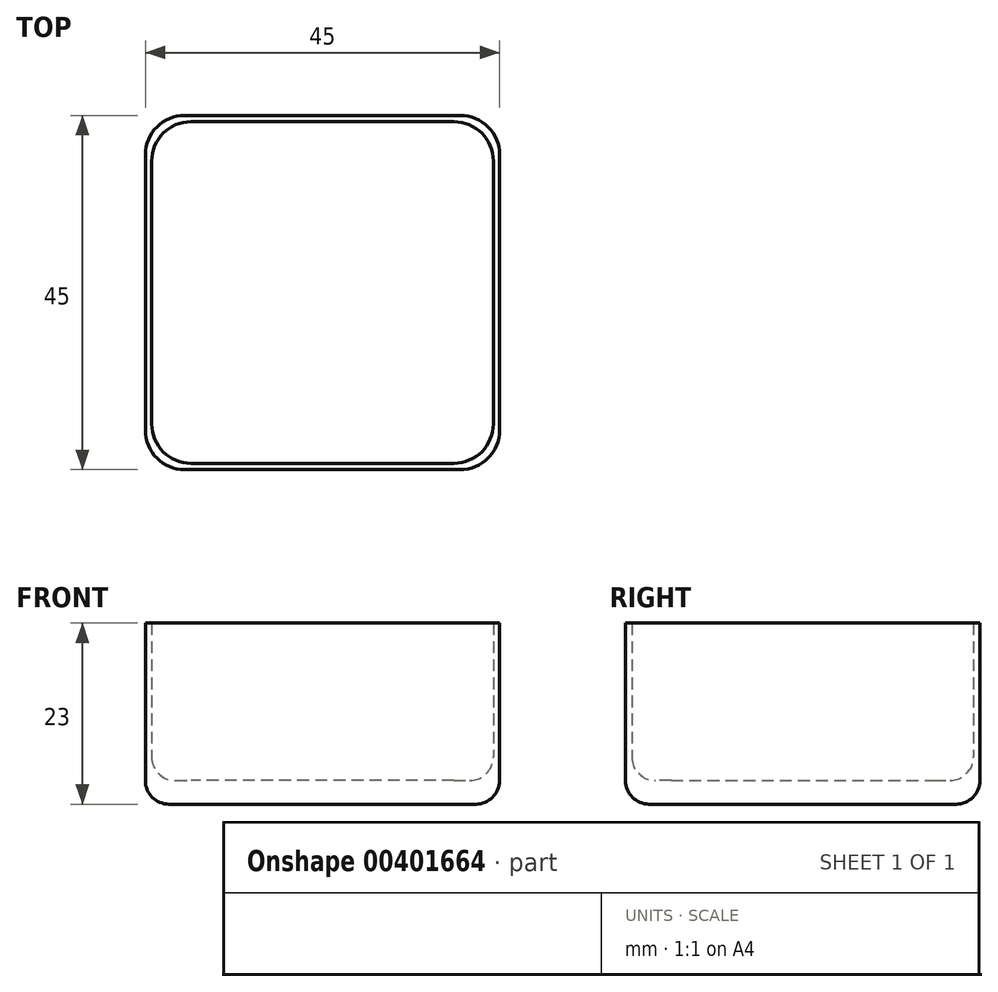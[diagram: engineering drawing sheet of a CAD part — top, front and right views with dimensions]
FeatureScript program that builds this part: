
annotation { "Feature Type Name" : "Feature", "Feature Type Description" : "" }
export const myFeature = defineFeature(function(context is Context, id is Id, definition is map)
    precondition{}
    {
        {
            var Q0;
            Q0=qCreatedBy(makeId("Top.planeOp"),FACE);
            var sketch = newSketch(context, id + "F0", { "sketchPlane" : qUnion([Q0])});
            skLineSegment(sketch, "E0.bottom", {"start": v(17.5, -22.5) * mm, "end": v(-17.5, -22.5) * mm});
            skLineSegment(sketch, "E0.top", {"start": v(17.5, 22.5) * mm, "end": v(-17.5, 22.5) * mm});
            skLineSegment(sketch, "E0.left", {"start": v(22.5, -17.5) * mm, "end": v(22.5, 17.5) * mm});
            skLineSegment(sketch, "E0.right", {"start": v(-22.5, -17.5) * mm, "end": v(-22.5, 17.5) * mm});
            skPoint(sketch, "E0.middle", {"position": v(0, 0) * mm});
            skPoint(sketch, "E1.visualSharp", {"position": v(-22.5, 22.5) * mm});
            skArc(sketch, "E1.filletArc", {"start": v(-17.5, 22.5) * mm, "mid": v(-21.04, 21.04) * mm, "end": v(-22.5, 17.5) * mm});
            skPoint(sketch, "E2.visualSharp", {"position": v(22.5, 22.5) * mm});
            skArc(sketch, "E2.filletArc", {"start": v(22.5, 17.5) * mm, "mid": v(21.04, 21.04) * mm, "end": v(17.5, 22.5) * mm});
            skPoint(sketch, "E3.visualSharp", {"position": v(22.5, -22.5) * mm});
            skArc(sketch, "E3.filletArc", {"start": v(17.5, -22.5) * mm, "mid": v(21.04, -21.04) * mm, "end": v(22.5, -17.5) * mm});
            skPoint(sketch, "E4.visualSharp", {"position": v(-22.5, -22.5) * mm});
            skArc(sketch, "E4.filletArc", {"start": v(-22.5, -17.5) * mm, "mid": v(-21.04, -21.04) * mm, "end": v(-17.5, -22.5) * mm});
            skLineSegment(sketch, "E5.0", {"start": v(-21.7, -16.7) * mm, "end": v(-21.7, 16.7) * mm});
            skLineSegment(sketch, "E5.1", {"start": v(16.7, -21.7) * mm, "end": v(-16.7, -21.7) * mm});
            skLineSegment(sketch, "E5.2", {"start": v(21.7, -16.7) * mm, "end": v(21.7, 16.7) * mm});
            skLineSegment(sketch, "E5.3", {"start": v(16.7, 21.7) * mm, "end": v(-16.7, 21.7) * mm});
            skPoint(sketch, "E6.visualSharp", {"position": v(-21.7, 21.7) * mm});
            skArc(sketch, "E6.filletArc", {"start": v(-16.7, 21.7) * mm, "mid": v(-20.24, 20.24) * mm, "end": v(-21.7, 16.7) * mm});
            skPoint(sketch, "E7.visualSharp", {"position": v(-21.7, -21.7) * mm});
            skArc(sketch, "E7.filletArc", {"start": v(-21.7, -16.7) * mm, "mid": v(-20.24, -20.24) * mm, "end": v(-16.7, -21.7) * mm});
            skPoint(sketch, "E8.visualSharp", {"position": v(21.7, -21.7) * mm});
            skArc(sketch, "E8.filletArc", {"start": v(16.7, -21.7) * mm, "mid": v(20.24, -20.24) * mm, "end": v(21.7, -16.7) * mm});
            skPoint(sketch, "E9.visualSharp", {"position": v(21.7, 21.7) * mm});
            skArc(sketch, "E9.filletArc", {"start": v(21.7, 16.7) * mm, "mid": v(20.24, 20.24) * mm, "end": v(16.7, 21.7) * mm});
            skSolve(sketch);
        }
        {
            var Q0;
            Q0 = qSketchRegion(id + "F0", true);
            extrude(context, id + "F1", {"entities" : qUnion([Q0]), "depth" : 20 * mm});
        }
        {
            var Q0;
            Q0=qCreatedBy(makeId("Top.planeOp"),FACE);
            var sketch = newSketch(context, id + "F2", { "sketchPlane" : qUnion([Q0])});
            skLineSegment(sketch, "E10.bottom", {"start": v(17.5, 22.5) * mm, "end": v(-17.5, 22.5) * mm});
            skLineSegment(sketch, "E10.top", {"start": v(17.5, -22.5) * mm, "end": v(-17.5, -22.5) * mm});
            skLineSegment(sketch, "E10.left", {"start": v(22.5, 17.5) * mm, "end": v(22.5, -17.5) * mm});
            skLineSegment(sketch, "E10.right", {"start": v(-22.5, 17.5) * mm, "end": v(-22.5, -17.5) * mm});
            skPoint(sketch, "E10.middle", {"position": v(0, 0) * mm});
            skPoint(sketch, "E11.visualSharp", {"position": v(-22.5, -22.5) * mm});
            skArc(sketch, "E11.filletArc", {"start": v(-22.5, -17.5) * mm, "mid": v(-21.04, -21.04) * mm, "end": v(-17.5, -22.5) * mm});
            skPoint(sketch, "E12.visualSharp", {"position": v(22.5, -22.5) * mm});
            skArc(sketch, "E12.filletArc", {"start": v(17.5, -22.5) * mm, "mid": v(21.04, -21.04) * mm, "end": v(22.5, -17.5) * mm});
            skPoint(sketch, "E13.visualSharp", {"position": v(22.5, 22.5) * mm});
            skArc(sketch, "E13.filletArc", {"start": v(22.5, 17.5) * mm, "mid": v(21.04, 21.04) * mm, "end": v(17.5, 22.5) * mm});
            skPoint(sketch, "E14.visualSharp", {"position": v(-22.5, 22.5) * mm});
            skArc(sketch, "E14.filletArc", {"start": v(-17.5, 22.5) * mm, "mid": v(-21.04, 21.04) * mm, "end": v(-22.5, 17.5) * mm});
            skSolve(sketch);
        }
        {
            var Q0;
            Q0 = qSketchRegion(id + "F2", true);
            extrude(context, id + "F3", {"entities" : qUnion([Q0]), "operationType" : NewBodyOperationType.ADD, "oppositeDirection" : true, "depth" : 3 * mm});
        }
        {
            var Q0;
            Q0=makeQuery(id+"F3.opExtrude","CAP_FACE",FACE,{"disambiguationData":[OSD([sQuery(id+"F2.wireOp",EDGE,"E10.bottom"),sQuery(id+"F2.wireOp",EDGE,"E10.top"),sQuery(id+"F2.wireOp",EDGE,"E10.left"),sQuery(id+"F2.wireOp",EDGE,"E10.right"),sQuery(id+"F2.wireOp",EDGE,"E11.filletArc"),sQuery(id+"F2.wireOp",EDGE,"E12.filletArc"),sQuery(id+"F2.wireOp",EDGE,"E13.filletArc"),sQuery(id+"F2.wireOp",EDGE,"E14.filletArc")])],"isStart":false});
            fillet(context, id + "F4", {"entities" : qUnion([Q0]), "radius" : 3 * mm, "tangentPropagation" : true, "allowEdgeOverflow" : false});
        }
        {
            var Q0;
            Q0=makeQuery(id+"F3.opExtrude","CAP_FACE",FACE,{"disambiguationData":[OSD([sQuery(id+"F2.wireOp",EDGE,"E10.bottom"),sQuery(id+"F2.wireOp",EDGE,"E10.top"),sQuery(id+"F2.wireOp",EDGE,"E10.left"),sQuery(id+"F2.wireOp",EDGE,"E10.right"),sQuery(id+"F2.wireOp",EDGE,"E11.filletArc"),sQuery(id+"F2.wireOp",EDGE,"E12.filletArc"),sQuery(id+"F2.wireOp",EDGE,"E13.filletArc"),sQuery(id+"F2.wireOp",EDGE,"E14.filletArc")])],"isStart":true});
            fillet(context, id + "F5", {"entities" : qUnion([Q0]), "radius" : 3 * mm, "tangentPropagation" : true, "allowEdgeOverflow" : false});
        }
    });
